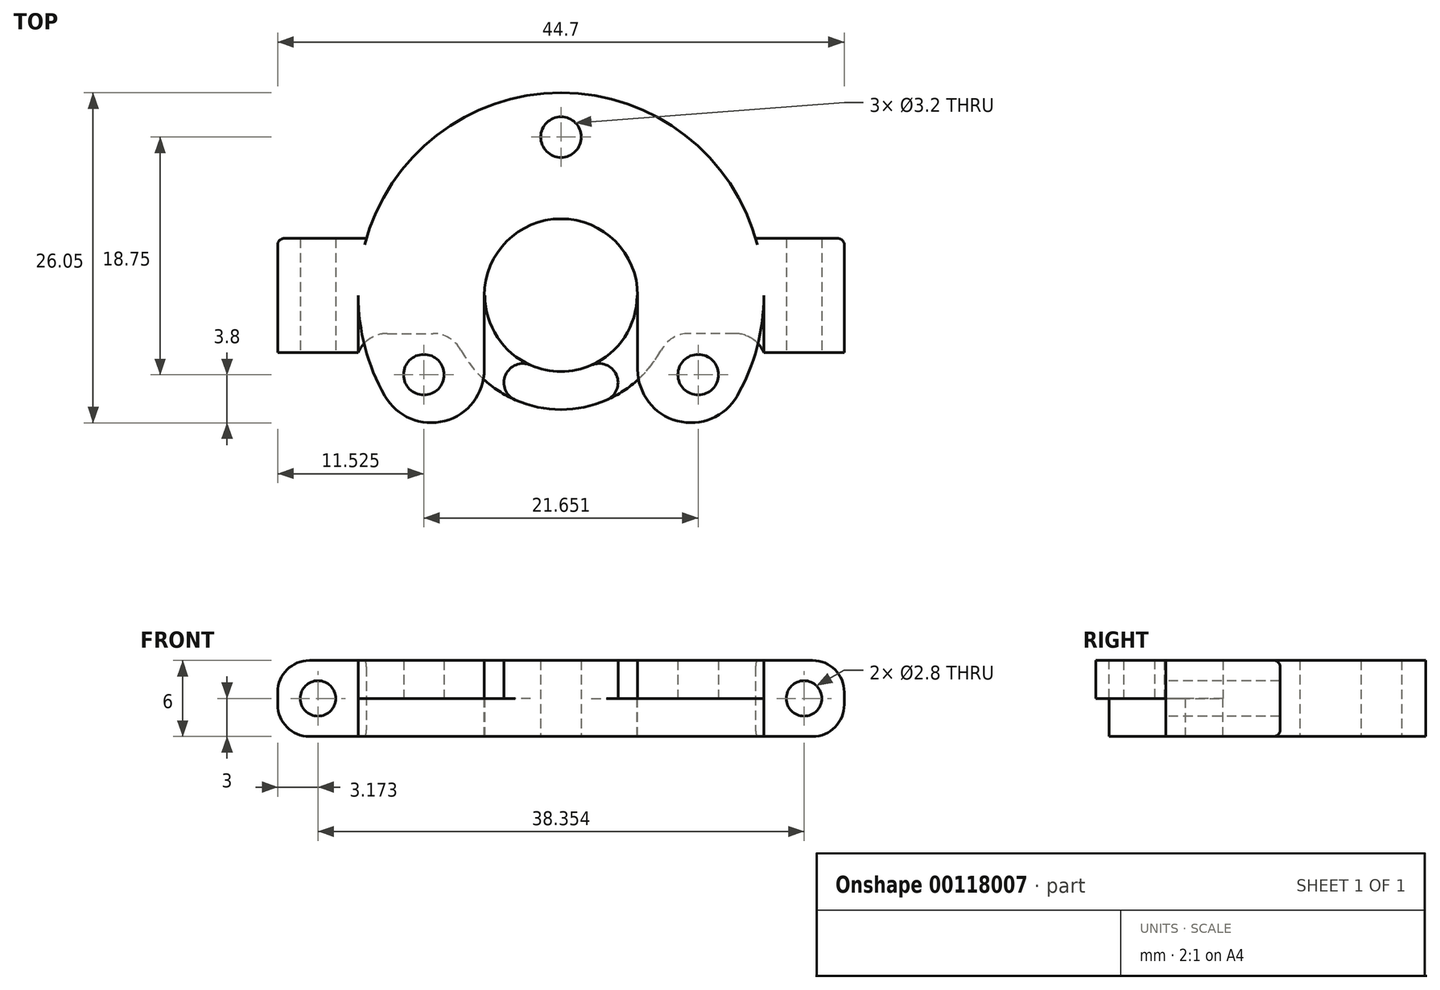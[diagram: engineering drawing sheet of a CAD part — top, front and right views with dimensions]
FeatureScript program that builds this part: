
annotation { "Feature Type Name" : "Feature", "Feature Type Description" : "" }
export const myFeature = defineFeature(function(context is Context, id is Id, definition is map)
    precondition{}
    {
        {
            var Q0;
            Q0=qCreatedBy(makeId("Top.planeOp"),FACE);
            var sketch = newSketch(context, id + "F0", { "sketchPlane" : qUnion([Q0])});
            skArc(sketch, "E0", {"start": v(6.05, -14.81) * mm, "mid": v(0, 16) * mm, "end": v(-6.05, -14.81) * mm});
            skLineSegment(sketch, "E1", {"start": v(0, 12.5) * mm, "end": v(0, 0) * mm, "construction": true});
            skLineSegment(sketch, "E2", {"start": v(0, 0) * mm, "end": v(-10.83, -6.25) * mm, "construction": true});
            skLineSegment(sketch, "E3", {"start": v(0, 0) * mm, "end": v(10.83, -6.25) * mm, "construction": true});
            skCircle(sketch, "E4", {"center": v(0, 12.5) * mm, "radius": 1.6 * mm});
            skCircle(sketch, "E5", {"center": v(10.83, -6.25) * mm, "radius": 1.6 * mm});
            skCircle(sketch, "E6", {"center": v(-10.83, -6.25) * mm, "radius": 1.6 * mm});
            skArc(sketch, "E7", {"start": v(6.05, 0) * mm, "mid": v(0, 6.05) * mm, "end": v(-6.05, 0) * mm});
            skArc(sketch, "E8", {"start": v(7.65, 0) * mm, "mid": v(0, 7.65) * mm, "end": v(-7.65, 0) * mm});
            skLineSegment(sketch, "E9", {"start": v(-6.05, 0) * mm, "end": v(-6.05, -14.81) * mm});
            skLineSegment(sketch, "E10", {"start": v(6.05, 0) * mm, "end": v(6.05, -14.81) * mm});
            skLineSegment(sketch, "E11", {"start": v(-16, 0) * mm, "end": v(16, 0) * mm});
            skLineSegment(sketch, "E12", {"start": v(-7.65, 0) * mm, "end": v(-6.05, 0) * mm});
            skLineSegment(sketch, "E13", {"start": v(6.05, 0) * mm, "end": v(7.65, 0) * mm});
            skLineSegment(sketch, "E14", {"start": v(16, 0) * mm, "end": v(22.35, 0) * mm});
            skLineSegment(sketch, "E15", {"start": v(22.35, 0) * mm, "end": v(22.35, 4.5) * mm});
            skLineSegment(sketch, "E16", {"start": v(22.35, 4.5) * mm, "end": v(15.35, 4.5) * mm});
            skLineSegment(sketch, "E17", {"start": v(-16, 0) * mm, "end": v(-22.35, 0) * mm});
            skLineSegment(sketch, "E18", {"start": v(-22.35, 0) * mm, "end": v(-22.35, 4.5) * mm});
            skLineSegment(sketch, "E19", {"start": v(-22.35, 4.5) * mm, "end": v(-15.35, 4.5) * mm});
            skCircle(sketch, "E20", {"center": v(-10.83, -6.25) * mm, "radius": 2.95 * mm, "construction": true});
            skSolve(sketch);
        }
        {
            var Q0;
            {var subQ0=sQuery(id+"F0.wireOp",EDGE,"E17");Q0=makeQuery(id+"F0.imprint","IMPRINT",FACE,{"disambiguationData":[TD([[makeQuery(id+"F0.imprint","IMPRINT",EDGE,{"derivedFrom":subQ0}),-1.0]])]});}
            var Q1;
            Q1=makeQuery(id+"F0.imprint","IMPRINT",FACE,{"disambiguationData":[TD([[makeQuery(id+"F0.imprint","IMPRINT",EDGE,{"derivedFrom":sQuery(id+"F0.wireOp",EDGE,"E4")}),-1.0]])]});
            var Q2;
            Q2=makeQuery(id+"F0.imprint","IMPRINT",FACE,{"disambiguationData":[TD([[makeQuery(id+"F0.imprint","IMPRINT",EDGE,{"derivedFrom":sQuery(id+"F0.wireOp",EDGE,"E7")}),-1.0]])]});
            var Q3;
            {var subQ0=sQuery(id+"F0.wireOp",EDGE,"E14");Q3=makeQuery(id+"F0.imprint","IMPRINT",FACE,{"disambiguationData":[TD([[makeQuery(id+"F0.imprint","IMPRINT",EDGE,{"derivedFrom":subQ0}),1.0]])]});}
            var Q4;
            Q4=makeQuery(id+"F0.imprint","IMPRINT",FACE,{"disambiguationData":[TD([[makeQuery(id+"F0.imprint","IMPRINT",EDGE,{"derivedFrom":sQuery(id+"F0.wireOp",EDGE,"E6")}),-1.0]])]});
            var Q5;
            Q5=makeQuery(id+"F0.imprint","IMPRINT",FACE,{"disambiguationData":[TD([[makeQuery(id+"F0.imprint","IMPRINT",EDGE,{"derivedFrom":sQuery(id+"F0.wireOp",EDGE,"E5")}),-1.0]])]});
            extrude(context, id + "F1", {"entities" : qUnion([Q0, Q1, Q2, Q3, Q4, Q5]), "depth" : 3 * mm});
        }
        {
            var Q0;
            Q0=makeQuery(id+"F0.imprint","IMPRINT",FACE,{"disambiguationData":[TD([[makeQuery(id+"F0.imprint","IMPRINT",EDGE,{"derivedFrom":sQuery(id+"F0.wireOp",EDGE,"E4")}),-1.0]])]});
            var Q1;
            Q1=makeQuery(id+"F0.imprint","IMPRINT",FACE,{"disambiguationData":[TD([[makeQuery(id+"F0.imprint","IMPRINT",EDGE,{"derivedFrom":sQuery(id+"F0.wireOp",EDGE,"E7")}),-1.0]])]});
            var Q2;
            {var subQ0=sQuery(id+"F0.wireOp",EDGE,"E14");Q2=makeQuery(id+"F0.imprint","IMPRINT",FACE,{"disambiguationData":[TD([[makeQuery(id+"F0.imprint","IMPRINT",EDGE,{"derivedFrom":subQ0}),1.0]])]});}
            var Q3;
            {var subQ0=sQuery(id+"F0.wireOp",EDGE,"E17");Q3=makeQuery(id+"F0.imprint","IMPRINT",FACE,{"disambiguationData":[TD([[makeQuery(id+"F0.imprint","IMPRINT",EDGE,{"derivedFrom":subQ0}),-1.0]])]});}
            extrude(context, id + "F2", {"entities" : qUnion([Q0, Q1, Q2, Q3]), "operationType" : NewBodyOperationType.ADD, "oppositeDirection" : true, "depth" : 3 * mm});
        }
        {
            var Q0;
            {var subQ0=sQuery(id+"F0.wireOp",EDGE,"E17");Q0=makeQuery(id+"F2.boolean.opBoolean","MERGE",FACE,{"derivedFrom":[makeQuery(id+"F1.opExtrude","SWEPT_FACE",FACE,{"disambiguationData":[OSD([subQ0])]}),makeQuery(id+"F2.opExtrude","SWEPT_FACE",FACE,{"disambiguationData":[OSD([sQuery(id+"F0.wireOp",EDGE,"E11"),sQuery(id+"F0.wireOp",EDGE,"E12"),subQ0])]})]});}
            var sketch = newSketch(context, id + "F3", { "sketchPlane" : qUnion([Q0])});
            skLineSegment(sketch, "E21", {"start": v(-16, 0) * mm, "end": v(-22.35, 0) * mm, "construction": true});
            skCircle(sketch, "E22", {"center": v(-19.18, 0) * mm, "radius": 1.4 * mm});
            skCircle(sketch, "E23", {"center": v(19.18, 0) * mm, "radius": 1.4 * mm});
            skLineSegment(sketch, "E24", {"start": v(0, 5.67) * mm, "end": v(0, -7.62) * mm, "construction": true});
            skCircle(sketch, "E25", {"center": v(-19.18, 0) * mm, "radius": 2.9 * mm, "construction": true});
            skSolve(sketch);
        }
        {
            var Q0;
            Q0=makeQuery(id+"F3.imprint","IMPRINT",FACE,{"disambiguationData":[TD([[makeQuery(id+"F3.imprint","IMPRINT",EDGE,{"derivedFrom":sQuery(id+"F3.wireOp",EDGE,"E23")}),1.0]])]});
            var Q1;
            Q1=makeQuery(id+"F3.imprint","IMPRINT",FACE,{"disambiguationData":[TD([[makeQuery(id+"F3.imprint","IMPRINT",EDGE,{"derivedFrom":sQuery(id+"F3.wireOp",EDGE,"E22")}),1.0]])]});
            extrude(context, id + "F4", {"entities" : qUnion([Q0, Q1]), "operationType" : NewBodyOperationType.REMOVE, "endBound" : BoundingType.THROUGH_ALL, "oppositeDirection" : true, "depth" : 25 * mm});
        }
        {
            var Q0;
            Q0=makeQuery(id+"F1.opExtrude","CAP_EDGE",EDGE,{"disambiguationData":[OSD([sQuery(id+"F0.wireOp",EDGE,"E18")])],"isStart":true});
            var Q1;
            Q1=makeQuery(id+"F1.opExtrude","CAP_EDGE",EDGE,{"disambiguationData":[OSD([sQuery(id+"F0.wireOp",EDGE,"E18")])],"isStart":false});
            var Q2;
            Q2=makeQuery(id+"F1.opExtrude","CAP_EDGE",EDGE,{"disambiguationData":[OSD([sQuery(id+"F0.wireOp",EDGE,"E15")])],"isStart":true});
            var Q3;
            Q3=makeQuery(id+"F1.opExtrude","CAP_EDGE",EDGE,{"disambiguationData":[OSD([sQuery(id+"F0.wireOp",EDGE,"E15")])],"isStart":false});
            var Q4;
            Q4=makeQuery(id+"F2.opExtrude","CAP_EDGE",EDGE,{"disambiguationData":[OSD([sQuery(id+"F0.wireOp",EDGE,"E18")])],"isStart":false});
            var Q5;
            Q5=makeQuery(id+"F2.opExtrude","CAP_EDGE",EDGE,{"disambiguationData":[OSD([sQuery(id+"F0.wireOp",EDGE,"E15")])],"isStart":false});
            fillet(context, id + "F5", {"entities" : qUnion([Q0, Q1, Q2, Q3, Q4, Q5]), "radius" : 2.5 * mm, "tangentPropagation" : true, "allowEdgeOverflow" : false});
        }
        {
            var Q0;
            Q0=makeQuery(id+"F1.opExtrude","CAP_EDGE",EDGE,{"disambiguationData":[OSD([sQuery(id+"F0.wireOp",EDGE,"E19")])],"isStart":false});
            var Q1;
            Q1=makeQuery(id+"F1.opExtrude","CAP_EDGE",EDGE,{"disambiguationData":[OSD([sQuery(id+"F0.wireOp",EDGE,"E16")])],"isStart":false});
            fillet(context, id + "F6", {"entities" : qUnion([Q0, Q1]), "radius" : .5 * mm, "tangentPropagation" : true, "allowEdgeOverflow" : false});
        }
        {
            var Q0;
            Q0=makeQuery(id+"F1.opExtrude","SWEPT_EDGE",EDGE,{"disambiguationData":[OSD([sQuery(id+"F0.wireOp",EDGE,"E0"),sQuery(id+"F0.wireOp",EDGE,"E9")])]});
            var Q1;
            Q1=makeQuery(id+"F1.opExtrude","SWEPT_EDGE",EDGE,{"disambiguationData":[OSD([sQuery(id+"F0.wireOp",EDGE,"E0"),sQuery(id+"F0.wireOp",EDGE,"E10")])]});
            fillet(context, id + "F7", {"entities" : qUnion([Q0, Q1]), "radius" : 4.2 * mm, "tangentPropagation" : true, "allowEdgeOverflow" : false});
        }
        {
            var Q0;
            Q0=qCreatedBy(makeId("Top.planeOp"),FACE);
            var sketch = newSketch(context, id + "F8", { "sketchPlane" : qUnion([Q0])});
            skArc(sketch, "E26", {"start": v(-6, 0) * mm, "mid": v(0, -6) * mm, "end": v(6, 0) * mm});
            skArc(sketch, "E27", {"start": v(-9, 0) * mm, "mid": v(0, -9) * mm, "end": v(9, 0) * mm});
            skLineSegment(sketch, "E28.0", {"start": v(-16, 0) * mm, "end": v(-22.35, 0) * mm});
            skLineSegment(sketch, "E28.1", {"start": v(-16, 0) * mm, "end": v(-6, 0) * mm});
            skLineSegment(sketch, "E28.2", {"start": v(16, 0) * mm, "end": v(22.35, 0) * mm});
            skLineSegment(sketch, "E29", {"start": v(-22.35, 0) * mm, "end": v(-22.35, -4.5) * mm});
            skLineSegment(sketch, "E30", {"start": v(-22.35, -4.5) * mm, "end": v(-16, -4.5) * mm});
            skLineSegment(sketch, "E31", {"start": v(-16, -4.5) * mm, "end": v(-16, -3) * mm});
            skLineSegment(sketch, "E32", {"start": v(-16, -3) * mm, "end": v(-8.49, -3) * mm});
            skLineSegment(sketch, "E33", {"start": v(22.35, 0) * mm, "end": v(22.35, -4.5) * mm});
            skLineSegment(sketch, "E34", {"start": v(22.35, -4.5) * mm, "end": v(16, -4.5) * mm});
            skLineSegment(sketch, "E35", {"start": v(16, -4.5) * mm, "end": v(16, -3) * mm});
            skLineSegment(sketch, "E36", {"start": v(16, -3) * mm, "end": v(8.49, -3) * mm});
            skLineSegment(sketch, "E37.0", {"start": v(-22.35, 0) * mm, "end": v(-22.35, 4.5) * mm, "construction": true});
            skLineSegment(sketch, "E38.trimOffspring", {"start": v(6, 0) * mm, "end": v(16, 0) * mm});
            skLineSegment(sketch, "E39", {"start": v(-16, -3) * mm, "end": v(-16, 0) * mm});
            skLineSegment(sketch, "E40", {"start": v(16, -3) * mm, "end": v(16, 0) * mm});
            skLineSegment(sketch, "E41", {"start": v(-4.5, -7.8) * mm, "end": v(-4.5, -3.97) * mm});
            skLineSegment(sketch, "E42", {"start": v(4.5, -7.8) * mm, "end": v(4.5, -3.97) * mm});
            skLineSegment(sketch, "E43", {"start": v(0, 0) * mm, "end": v(0, -11.2) * mm, "construction": true});
            skSolve(sketch);
        }
        {
            var Q0;
            Q0=qSketchRegion(id+"F8",true);
            extrude(context, id + "F9", {"entities" : qUnion([Q0]), "oppositeDirection" : true, "depth" : 3 * mm});
        }
        {
            var Q0;
            Q0=makeQuery(id+"F8.imprint","IMPRINT",FACE,{"disambiguationData":[TD([[makeQuery(id+"F8.imprint","IMPRINT",EDGE,{"derivedFrom":sQuery(id+"F8.wireOp",EDGE,"E28.0")}),1.0]])]});
            var Q1;
            Q1=makeQuery(id+"F8.imprint","IMPRINT",FACE,{"disambiguationData":[TD([[makeQuery(id+"F8.imprint","IMPRINT",EDGE,{"derivedFrom":sQuery(id+"F8.wireOp",EDGE,"E28.2")}),-1.0]])]});
            var Q2;
            {var subQ0=sQuery(id+"F8.wireOp",EDGE,"E41");Q2=makeQuery(id+"F8.imprint","IMPRINT",FACE,{"disambiguationData":[TD([[makeQuery(id+"F8.imprint","IMPRINT",EDGE,{"derivedFrom":subQ0}),-1.0]])]});}
            extrude(context, id + "F10", {"entities" : qUnion([Q0, Q1, Q2]), "operationType" : NewBodyOperationType.ADD, "depth" : 3 * mm});
        }
        {
            var Q0;
            {var subQ0=sQuery(id+"F8.wireOp",EDGE,"E30");Q0=makeQuery(id+"F10.boolean.opBoolean","MERGE",FACE,{"derivedFrom":[makeQuery(id+"F9.opExtrude","SWEPT_FACE",FACE,{"disambiguationData":[OSD([subQ0])]}),makeQuery(id+"F10.opExtrude","SWEPT_FACE",FACE,{"disambiguationData":[OSD([subQ0])]})]});}
            var sketch = newSketch(context, id + "F11", { "sketchPlane" : qUnion([Q0])});
            skLineSegment(sketch, "E44", {"start": v(-22.35, 0) * mm, "end": v(-16, 0) * mm, "construction": true});
            skLineSegment(sketch, "E45", {"start": v(0, -3.32) * mm, "end": v(0, 4.53) * mm, "construction": true});
            skCircle(sketch, "E46", {"center": v(-19.18, 0) * mm, "radius": 1.4 * mm});
            skCircle(sketch, "E47", {"center": v(19.18, 0) * mm, "radius": 1.4 * mm});
            skSolve(sketch);
        }
        {
            var Q0;
            Q0=makeQuery(id+"F11.imprint","IMPRINT",FACE,{"disambiguationData":[TD([[makeQuery(id+"F11.imprint","IMPRINT",EDGE,{"derivedFrom":sQuery(id+"F11.wireOp",EDGE,"E46")}),1.0]])]});
            var Q1;
            Q1=makeQuery(id+"F11.imprint","IMPRINT",FACE,{"disambiguationData":[TD([[makeQuery(id+"F11.imprint","IMPRINT",EDGE,{"derivedFrom":sQuery(id+"F11.wireOp",EDGE,"E47")}),1.0]])]});
            extrude(context, id + "F12", {"entities" : qUnion([Q0, Q1]), "operationType" : NewBodyOperationType.REMOVE, "oppositeDirection" : true, "depth" : 25 * mm});
        }
        {
            var Q0;
            Q0=makeQuery(id+"F9.opExtrude","SWEPT_EDGE",EDGE,{"disambiguationData":[OSD([sQuery(id+"F8.wireOp",EDGE,"E31"),sQuery(id+"F8.wireOp",EDGE,"E32"),sQuery(id+"F8.wireOp",EDGE,"E39")])]});
            var Q1;
            Q1=makeQuery(id+"F9.opExtrude","SWEPT_EDGE",EDGE,{"disambiguationData":[OSD([sQuery(id+"F8.wireOp",EDGE,"E35"),sQuery(id+"F8.wireOp",EDGE,"E36"),sQuery(id+"F8.wireOp",EDGE,"E40")])]});
            var Q2;
            Q2=makeQuery(id+"F9.opExtrude","SWEPT_EDGE",EDGE,{"disambiguationData":[OSD([sQuery(id+"F8.wireOp",EDGE,"E27"),sQuery(id+"F8.wireOp",EDGE,"E32")])]});
            var Q3;
            Q3=makeQuery(id+"F9.opExtrude","SWEPT_EDGE",EDGE,{"disambiguationData":[OSD([sQuery(id+"F8.wireOp",EDGE,"E27"),sQuery(id+"F8.wireOp",EDGE,"E36")])]});
            var Q4;
            Q4=makeQuery(id+"F9.opExtrude","CAP_EDGE",EDGE,{"disambiguationData":[OSD([sQuery(id+"F8.wireOp",EDGE,"E33")])],"isStart":false});
            var Q5;
            Q5=makeQuery(id+"F10.opExtrude","CAP_EDGE",EDGE,{"disambiguationData":[OSD([sQuery(id+"F8.wireOp",EDGE,"E33")])],"isStart":false});
            var Q6;
            Q6=makeQuery(id+"F10.opExtrude","CAP_EDGE",EDGE,{"disambiguationData":[OSD([sQuery(id+"F8.wireOp",EDGE,"E29")])],"isStart":false});
            var Q7;
            Q7=makeQuery(id+"F9.opExtrude","CAP_EDGE",EDGE,{"disambiguationData":[OSD([sQuery(id+"F8.wireOp",EDGE,"E29")])],"isStart":false});
            fillet(context, id + "F13", {"entities" : qUnion([Q0, Q1, Q2, Q3, Q4, Q5, Q6, Q7]), "radius" : 2.5 * mm, "tangentPropagation" : true, "allowEdgeOverflow" : false});
        }
        {
            var Q0;
            Q0=makeQuery(id+"F10.opExtrude","SWEPT_EDGE",EDGE,{"disambiguationData":[OSD([sQuery(id+"F8.wireOp",EDGE,"E26"),sQuery(id+"F8.wireOp",EDGE,"E41")])]});
            var Q1;
            Q1=makeQuery(id+"F10.opExtrude","SWEPT_EDGE",EDGE,{"disambiguationData":[OSD([sQuery(id+"F8.wireOp",EDGE,"E26"),sQuery(id+"F8.wireOp",EDGE,"E42")])]});
            var Q2;
            Q2=makeQuery(id+"F10.opExtrude","SWEPT_EDGE",EDGE,{"disambiguationData":[OSD([sQuery(id+"F8.wireOp",EDGE,"E27"),sQuery(id+"F8.wireOp",EDGE,"E41")])]});
            var Q3;
            Q3=makeQuery(id+"F10.opExtrude","SWEPT_EDGE",EDGE,{"disambiguationData":[OSD([sQuery(id+"F8.wireOp",EDGE,"E27"),sQuery(id+"F8.wireOp",EDGE,"E42")])]});
            fillet(context, id + "F14", {"entities" : qUnion([Q0, Q1, Q2, Q3]), "radius" : 1.5 * mm, "tangentPropagation" : true, "allowEdgeOverflow" : false});
        }
    });
